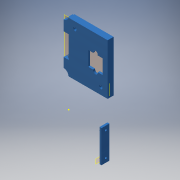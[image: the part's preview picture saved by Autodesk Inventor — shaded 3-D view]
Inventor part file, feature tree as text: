
AUTODESK INVENTOR PART (.ipt)
format: ipt  version: 2017 (Build 210142000, 142)  size: 319,488 bytes
history: native  units: in
note: dims shown in document units (in); Inventor stores cm internally (conversion verified against a paired STEP export)
features: reference x17, sketch x9, extrude x8, other x7, plane x6, fillet x2, projected_geometry x2, chamfer x1
ambient origin geometry x8: Origin, YZ Plane, XZ Plane, XY Plane, X Axis, Y Axis, Z Axis, Center Point
bodies: Solid1 (feature_tree)
feature tree (52):
  plane  "Work Plane1"
  sketch  "Sketch1"  dims[d0=0.05in d1=1.0in d2=0.0in]
  plane  "Work Plane2"
  plane  "Work Plane4"
  extrude  "Extrusion1"  Depth=0.05in TaperAngle=0.0deg
  plane  "Work Plane3"
  extrude  "Extrusion3"  Depth=0.1in
  extrude  "Extrusion4"  Depth=0.2in TaperAngle=0.0deg
  chamfer  "Chamfer1"  Distance=0.025in Angle=45.0deg
  extrude  "Extrusion5"  Depth=0.1in
  extrude  "Extrusion6"  Depth=0.25in
  fillet  "Fillet1"  Radius=0.025in
  extrude  "Extrusion7"  Depth=0.05in
  fillet  "Fillet2"  Radius=0.1in
  plane  "Work Plane5"
  extrude  "Extrusion8"  Depth=0.03in
  sketch  "Sketch9"  dims[d28=0.1in d29=0.03in]
  plane  "Work Plane6"
  extrude  "Extrusion9"  Depth=0.1in TaperAngle=0.0deg
  sketch  "Sketch10"  dims[d30=0.1in d31=0.1in d32=0.0in d33=0.1in d34=0.1in d35=0.0in]
  reference  "Reference1"
  sketch  "Sketch2"  dims[d5=0.1in d6=0.0in d7=0.1in]
  reference  "Reference2"
  reference  "Reference3"
  reference  "Reference4"
  reference  "Reference5"
  reference  "Reference6"
  reference  "Reference7"
  sketch  "Sketch3"  dims[d8=0.1in d9=0.2in d10=0.0in]
  reference  "Reference8"
  reference  "Reference9"
  sketch  "Sketch5"  dims[d11=0.03in d12=0.025in d13=0.125in d14=45.0deg]
  reference  "Reference10"
  reference  "Reference11"
  reference  "Reference12"
  reference  "Reference13"
  sketch  "Sketch6"  dims[d15=1.0in d16=0.0in d17=0.1in]
  sketch  "Sketch7"  dims[d18=0.35in d19=0.0in d20=0.25in d21=0.025in]
  reference  "Reference14"
  reference  "Reference15"
  sketch  "Sketch8"  dims[d22=0.25in d23=0.0in d24=0.05in d27=0.1in]
  reference  "Reference16"
  reference  "Reference17"
  projected_geometry  "Projected Loop1"
  projected_geometry  "Projected Loop2"
  other  "<userpath>\Documents\Inventor\PixyCam and Gimbal\Assembly2.iam"
  other  "Assembly2.iam"
  other  "PixyCamKinda:1"
  other  "backCase:1"
  other  "servo arm:1"
  other  "OtherCamera:1"
  other  "<userpath>\Documents\Inventor\PixyCam and Gimbal\Assembly2.iam"
